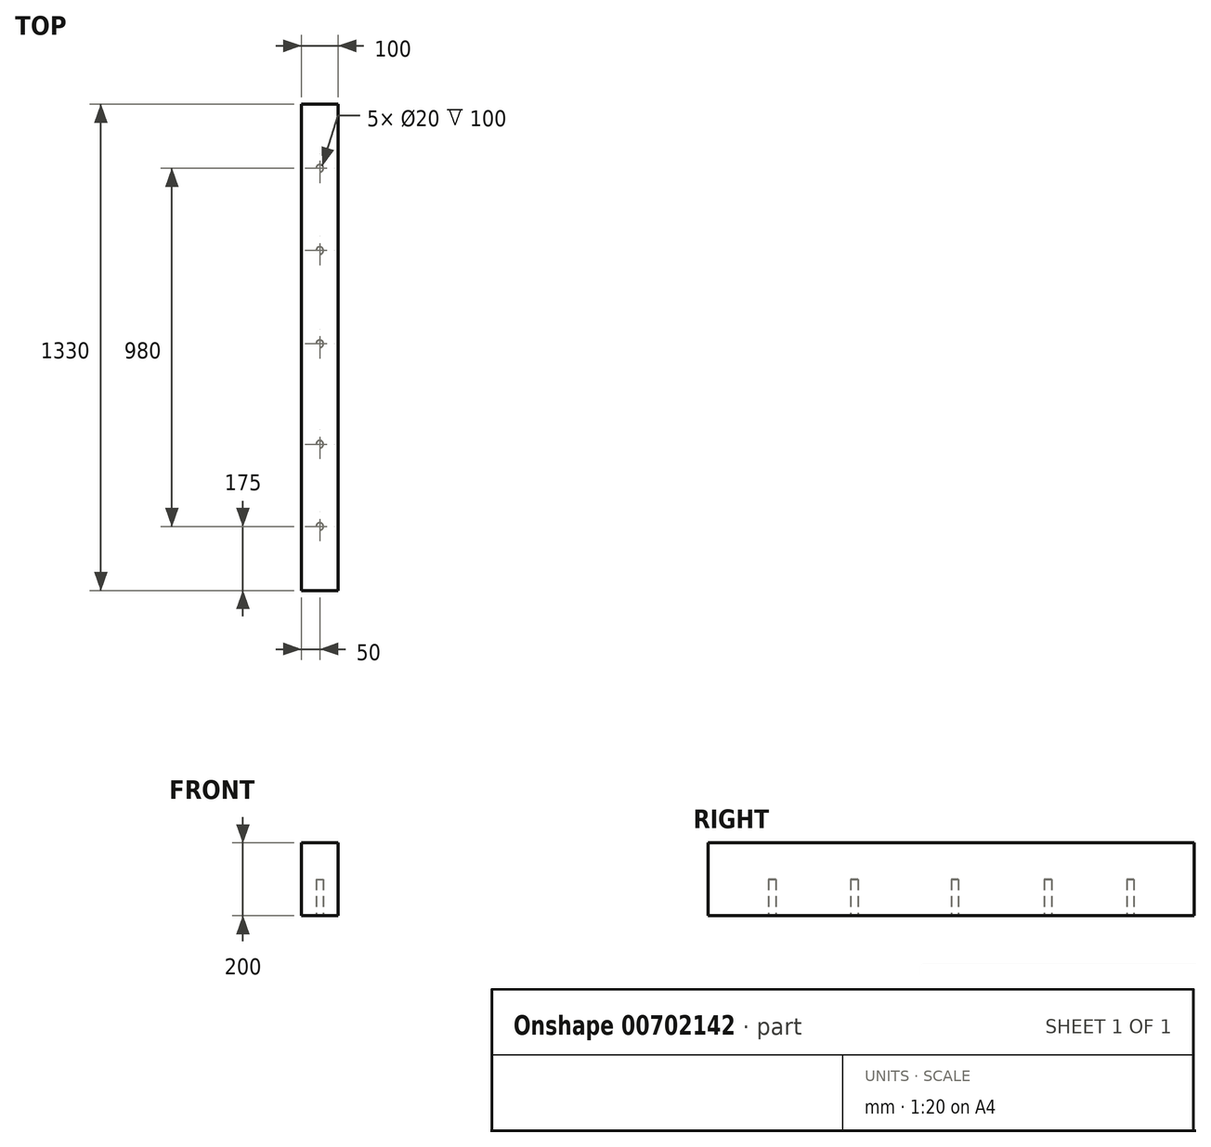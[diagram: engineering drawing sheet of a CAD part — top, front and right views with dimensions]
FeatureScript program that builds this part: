
annotation { "Feature Type Name" : "Feature", "Feature Type Description" : "" }
export const myFeature = defineFeature(function(context is Context, id is Id, definition is map)
    precondition{}
    {
        {
            var Q0;
            Q0=qCreatedBy(makeId("Front.planeOp"),FACE);
            var sketch = newSketch(context, id + "F0", { "sketchPlane" : qUnion([Q0])});
            skLineSegment(sketch, "E0.bottom", {"start": v(0, 0) * mm, "end": v(-100, 0) * mm});
            skLineSegment(sketch, "E0.top", {"start": v(0, 200) * mm, "end": v(-100, 200) * mm});
            skLineSegment(sketch, "E0.left", {"start": v(0, 0) * mm, "end": v(0, 200) * mm});
            skLineSegment(sketch, "E0.right", {"start": v(-100, 0) * mm, "end": v(-100, 200) * mm});
            skSolve(sketch);
        }
        {
            var Q0;
            Q0=qSketchRegion(id+"F0",true);
            extrude(context, id + "F1", {"entities" : qUnion([Q0]), "depth" : 1330 * mm, "offsetDistance" : 25 * mm});
        }
        {
            var Q0;
            Q0=makeQuery(id+"F1.opExtrude","SWEPT_FACE",FACE,{"disambiguationData":[OSD([sQuery(id+"F0.wireOp",EDGE,"E0.bottom")])]});
            var sketch = newSketch(context, id + "F2", { "sketchPlane" : qUnion([Q0])});
            skCircle(sketch, "E1", {"center": v(-50, 1155) * mm, "radius": 10 * mm});
            skPoint(sketch, "E1.centerSnap0", {"position": v(-50, 1330) * mm});
            skCircle(sketch, "E2", {"center": v(-50, 930) * mm, "radius": 10 * mm});
            skCircle(sketch, "E3", {"center": v(-50, 655) * mm, "radius": 10 * mm});
            skCircle(sketch, "E4", {"center": v(-50, 400) * mm, "radius": 10 * mm});
            skCircle(sketch, "E5", {"center": v(-50, 175) * mm, "radius": 10 * mm});
            skSolve(sketch);
        }
        {
            var Q0;
            Q0=qSketchRegion(id+"F2",true);
            extrude(context, id + "F3", {"entities" : qUnion([Q0]), "operationType" : NewBodyOperationType.REMOVE, "oppositeDirection" : true, "depth" : 100 * mm, "offsetDistance" : 25 * mm});
        }
    });
